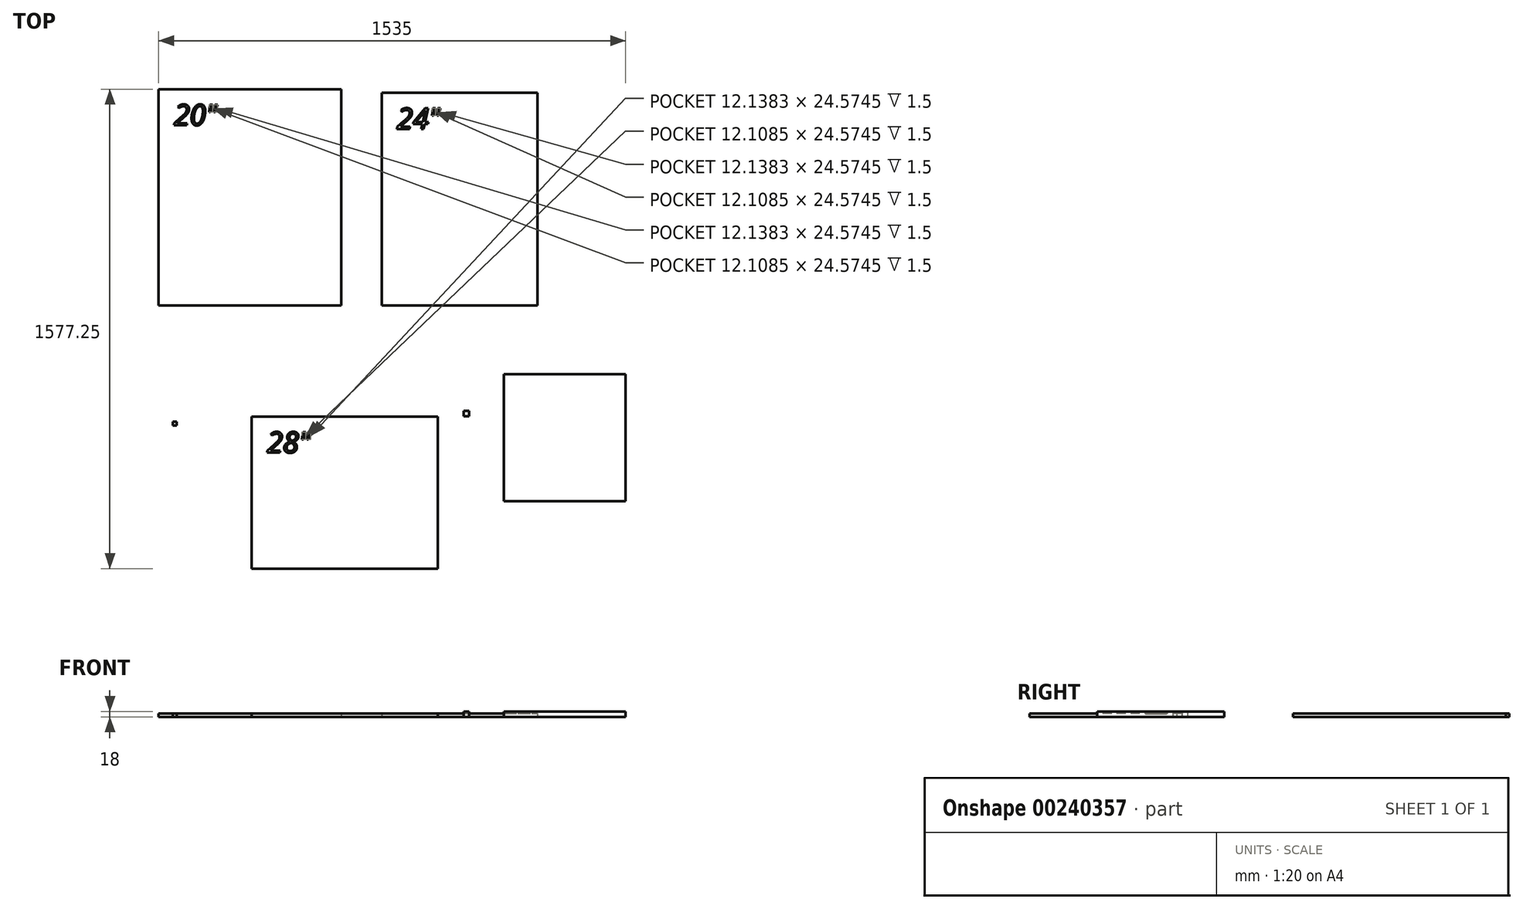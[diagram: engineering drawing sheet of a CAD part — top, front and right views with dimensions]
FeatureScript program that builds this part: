
annotation { "Feature Type Name" : "Feature", "Feature Type Description" : "" }
export const myFeature = defineFeature(function(context is Context, id is Id, definition is map)
    precondition{}
    {
        {
            var Q0;
            Q0=qCreatedBy(makeId("Top.planeOp"),FACE);
            var sketch = newSketch(context, id + "F0", { "sketchPlane" : qUnion([Q0])});
            skLineSegment(sketch, "E0.bottom", {"start": v(0, 0) * mm, "end": v(-600, 0) * mm});
            skLineSegment(sketch, "E0.top", {"start": v(0, 712) * mm, "end": v(-600, 712) * mm});
            skLineSegment(sketch, "E0.left", {"start": v(0, 0) * mm, "end": v(0, 712) * mm});
            skLineSegment(sketch, "E0.right", {"start": v(-600, 0) * mm, "end": v(-600, 712) * mm});
            skSolve(sketch);
        }
        {
            var Q0;
            Q0 = qSketchRegion(id + "F0", true);
            extrude(context, id + "F1", {"entities" : qUnion([Q0]), "depth" : 12 * mm});
        }
        {
            var Q0;
            Q0=qCreatedBy(makeId("Top.planeOp"),FACE);
            var sketch = newSketch(context, id + "F2", { "sketchPlane" : qUnion([Q0])});
            skLineSegment(sketch, "E1.bottom", {"start": v(133.15, 700) * mm, "end": v(645.15, 700) * mm});
            skLineSegment(sketch, "E1.top", {"start": v(133.15, 0) * mm, "end": v(645.15, 0) * mm});
            skLineSegment(sketch, "E1.left", {"start": v(133.15, 700) * mm, "end": v(133.15, 0) * mm});
            skLineSegment(sketch, "E1.right", {"start": v(645.15, 700) * mm, "end": v(645.15, 0) * mm});
            skSolve(sketch);
        }
        {
            var Q0;
            Q0 = qSketchRegion(id + "F2", true);
            extrude(context, id + "F3", {"entities" : qUnion([Q0]), "depth" : 12 * mm});
        }
        {
            var Q0;
            Q0=qCreatedBy(makeId("Top.planeOp"),FACE);
            var sketch = newSketch(context, id + "F4", { "sketchPlane" : qUnion([Q0])});
            skLineSegment(sketch, "E2.bottom", {"start": v(-294.3, -365.25) * mm, "end": v(317.7, -365.25) * mm});
            skLineSegment(sketch, "E2.top", {"start": v(-294.3, -865.25) * mm, "end": v(317.7, -865.25) * mm});
            skLineSegment(sketch, "E2.left", {"start": v(-294.3, -365.25) * mm, "end": v(-294.3, -865.25) * mm});
            skLineSegment(sketch, "E2.right", {"start": v(317.7, -365.25) * mm, "end": v(317.7, -865.25) * mm});
            skSolve(sketch);
        }
        {
            var Q0;
            Q0 = qSketchRegion(id + "F4", true);
            extrude(context, id + "F5", {"entities" : qUnion([Q0]), "depth" : 12 * mm});
        }
        {
            var Q0;
            Q0=qCreatedBy(makeId("Top.planeOp"),FACE);
            var sketch = newSketch(context, id + "F6", { "sketchPlane" : qUnion([Q0])});
            skLineSegment(sketch, "E3.bottom", {"start": v(-553.01, -382.26) * mm, "end": v(-541.01, -382.26) * mm});
            skLineSegment(sketch, "E3.top", {"start": v(-553.01, -394.26) * mm, "end": v(-541.01, -394.26) * mm});
            skLineSegment(sketch, "E3.left", {"start": v(-553.01, -382.26) * mm, "end": v(-553.01, -394.26) * mm});
            skLineSegment(sketch, "E3.right", {"start": v(-541.01, -382.26) * mm, "end": v(-541.01, -394.26) * mm});
            skSolve(sketch);
        }
        {
            var Q0;
            Q0 = qSketchRegion(id + "F6", true);
            extrude(context, id + "F7", {"entities" : qUnion([Q0]), "depth" : 12 * mm});
        }
        {
            var Q0;
            Q0=makeQuery(id+"F1.opExtrude","CAP_FACE",FACE,{"disambiguationData":[OSD([sQuery(id+"F0.wireOp",EDGE,"E0.bottom"),sQuery(id+"F0.wireOp",EDGE,"E0.top"),sQuery(id+"F0.wireOp",EDGE,"E0.left"),sQuery(id+"F0.wireOp",EDGE,"E0.right")])],"isStart":false});
            var sketch = newSketch(context, id + "F8", { "sketchPlane" : qUnion([Q0])});
            skText(sketch, "E4", { "text": "20\"", "fontName": "OpenSans-Italic.ttf"});
            const initialGuessF8  = {"E4": [-0.55, 0.59337, 1, 0, 0.06863]};
            skSetInitialGuess(sketch, initialGuessF8);
            skSolve(sketch);
        }
        {
            var Q0;
            Q0 = qSketchRegion(id + "F8", true);
            extrude(context, id + "F9", {"entities" : qUnion([Q0]), "operationType" : NewBodyOperationType.REMOVE, "oppositeDirection" : true, "depth" : 1.5 * mm});
        }
        {
            var Q0;
            Q0=makeQuery(id+"F3.opExtrude","CAP_FACE",FACE,{"disambiguationData":[OSD([sQuery(id+"F2.wireOp",EDGE,"E1.bottom"),sQuery(id+"F2.wireOp",EDGE,"E1.top"),sQuery(id+"F2.wireOp",EDGE,"E1.left"),sQuery(id+"F2.wireOp",EDGE,"E1.right")])],"isStart":false});
            var sketch = newSketch(context, id + "F10", { "sketchPlane" : qUnion([Q0])});
            skText(sketch, "E5", { "text": "24\"", "fontName": "OpenSans-Italic.ttf"});
            const initialGuessF10  = {"E5": [0.18315, 0.58137, 1, 0, 0.06863]};
            skSetInitialGuess(sketch, initialGuessF10);
            skSolve(sketch);
        }
        {
            var Q0;
            Q0 = qSketchRegion(id + "F10", true);
            extrude(context, id + "F11", {"entities" : qUnion([Q0]), "operationType" : NewBodyOperationType.REMOVE, "oppositeDirection" : true, "depth" : 1.5 * mm});
        }
        {
            var Q0;
            Q0=makeQuery(id+"F5.opExtrude","CAP_FACE",FACE,{"disambiguationData":[OSD([sQuery(id+"F4.wireOp",EDGE,"E2.bottom"),sQuery(id+"F4.wireOp",EDGE,"E2.top"),sQuery(id+"F4.wireOp",EDGE,"E2.left"),sQuery(id+"F4.wireOp",EDGE,"E2.right")])],"isStart":false});
            var sketch = newSketch(context, id + "F12", { "sketchPlane" : qUnion([Q0])});
            skText(sketch, "E6", { "text": "28\"", "fontName": "OpenSans-Italic.ttf"});
            const initialGuessF12  = {"E6": [-0.2443, -0.48389, 1, 0, 0.06863]};
            skSetInitialGuess(sketch, initialGuessF12);
            skSolve(sketch);
        }
        {
            var Q0;
            Q0 = qSketchRegion(id + "F12", true);
            extrude(context, id + "F13", {"entities" : qUnion([Q0]), "operationType" : NewBodyOperationType.REMOVE, "oppositeDirection" : true, "depth" : 1.5 * mm});
        }
        {
            var Q0;
            Q0=qCreatedBy(makeId("Top.planeOp"),FACE);
            var sketch = newSketch(context, id + "F14", { "sketchPlane" : qUnion([Q0])});
            skLineSegment(sketch, "E7.bottom", {"start": v(535, -225) * mm, "end": v(935, -225) * mm});
            skLineSegment(sketch, "E7.top", {"start": v(535, -643) * mm, "end": v(935, -643) * mm});
            skLineSegment(sketch, "E7.left", {"start": v(535, -225) * mm, "end": v(535, -643) * mm});
            skLineSegment(sketch, "E7.right", {"start": v(935, -225) * mm, "end": v(935, -643) * mm});
            skSolve(sketch);
        }
        {
            var Q0;
            Q0 = qSketchRegion(id + "F14", true);
            extrude(context, id + "F15", {"entities" : qUnion([Q0]), "depth" : 18 * mm});
        }
        {
            var Q0;
            Q0=qCreatedBy(makeId("Top.planeOp"),FACE);
            var sketch = newSketch(context, id + "F16", { "sketchPlane" : qUnion([Q0])});
            skLineSegment(sketch, "E8.bottom", {"start": v(402.65, -346.25) * mm, "end": v(420.65, -346.25) * mm});
            skLineSegment(sketch, "E8.top", {"start": v(402.65, -364.25) * mm, "end": v(420.65, -364.25) * mm});
            skLineSegment(sketch, "E8.left", {"start": v(402.65, -346.25) * mm, "end": v(402.65, -364.25) * mm});
            skLineSegment(sketch, "E8.right", {"start": v(420.65, -346.25) * mm, "end": v(420.65, -364.25) * mm});
            skSolve(sketch);
        }
        {
            var Q0;
            Q0 = qSketchRegion(id + "F16", true);
            extrude(context, id + "F17", {"entities" : qUnion([Q0]), "depth" : 18 * mm});
        }
    });
